# Revit family: F1760-FL
name_source: partatom
category: Plumbing Fixtures
revit_build: Autodesk Revit 2018 (Build: 20170223_1515(x64)
units: mm (PartAtom-declared; Revit-internal decimal feet)

## family parameters
Cut with Voids When Loaded = No
Host = Face
Part Type = Normal
Room Calculation Point = No
Round Connector Dimension = Use Radius
Shared = No

## types (5) — shared parameters
Default Elevation = 0' - 0"
Floor Drain Material = Paint - Sherwin Williams Paint - #952C2A - Bellwood Red
Manufacturer = MIFAB
URL = WWW.MIFAB.COM
zero-valued in all types: CWFU, WFU

## per-type parameters (varying)
| type | Body Height | Description | Model | Pipe Diameter | Pipe Radius | Top Assembly Adjustment |
| Pipe Size-Ø2" | 0' - 5 3/4" | FLOOR DRAIN WITH 16” SQUARE ADJUSTABLE TRACTOR GRATE & SIPHONIC TO GRAVITY BREAK AREA DRAIN | MH-F1460 | 0' - 2" | 0' - 1" | 0' - 6" |
| Pipe Size-Ø3" | 0' - 5 3/4" | FLOOR DRAIN WITH 16” SQUARE ADJUSTABLE TRACTOR GRATE & SIPHONIC TO GRAVITY BREAK AREA DRAIN | MH-F1460 | 0' - 3" | 0' - 1 1/2" | 0' - 6" |
| Pipe Size-Ø4" | 0' - 5 3/4" | 7" x 15" HEAVY DUTY GUTTER DRAIN WITH ANCHOR FLANGE | F1760-FL | 0' - 4" | 0' - 2" | 0' - 6" |
| Pipe Size-Ø5" | 0' - 5 3/4" | FLOOR DRAIN WITH 16” SQUARE ADJUSTABLE TRACTOR GRATE & SIPHONIC TO GRAVITY BREAK AREA DRAIN | MH-F1460 | 0' - 5" | 0' - 2 1/2" | 0' - 6" |
| Pipe Size-Ø6" | 0' - 7 1/4" | FLOOR DRAIN WITH 16” SQUARE ADJUSTABLE TRACTOR GRATE & SIPHONIC TO GRAVITY BREAK AREA DRAIN | MH-F1460 | 0' - 6" | 0' - 3" | 0' - 7 1/4" |

## geometry (parser evidence)
native form markers: Blend x2, Sweep x5
no freeform markers — native parametric forms only
